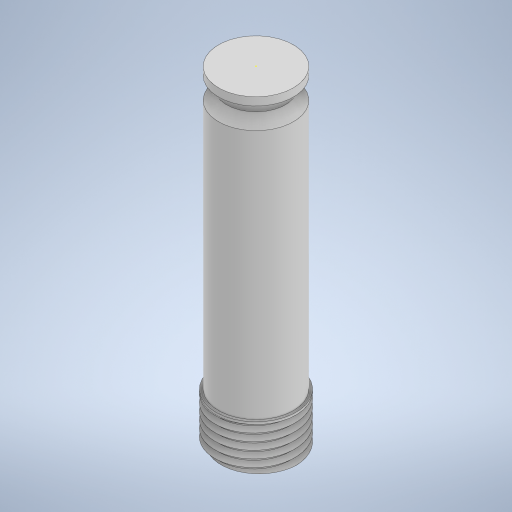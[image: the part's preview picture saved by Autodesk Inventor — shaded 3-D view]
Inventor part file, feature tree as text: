
AUTODESK INVENTOR PART (.ipt)
format: ipt  version: 2024 (Build 280153000, 153)  size: 430,080 bytes
history: native  units: mm
features: sketch x8, extrude x5, other x1, pattern_circular x1, revolve x1
ambient origin geometry x8: Origin, YZ Plane, XZ Plane, XY Plane, X Axis, Y Axis, Z Axis, Center Point
bodies: Volumenkörper1 (feature_tree)
feature tree (16):
  extrude  "Extrusion1"  Depth=61.0mm TaperAngle=0.0deg
  other  "Spirale1"
  extrude  "Extrusion9"  Depth=0.5mm
  extrude  "Extrusion6"  Depth=21.85mm
  pattern_circular  "Runde Anordnung1"  Count=4  [1 undecoded]
  extrude  "Extrusion10"  Depth=15.0mm
  extrude  "Extrusion11"  Depth=10.0mm
  revolve  "Umdrehung1"
  sketch  "Skizze18"  dims[d71=60.0deg d72=0.2mm d73=7.5mm d75=14.5mm d76=15.0mm d77=27.0mm d78=21.85mm d79=0.0mm d80=0.0mm d86=60.0mm d87=0.0mm d89=1.5mm d90=4.0mm d91=1.5mm d52=0.0mm d53=0.0mm d55=0.0mm]
  sketch  "Skizze1"  dims[d0=15.0mm d1=61.0mm d2=0.0mm]
  sketch  "Skizze6"  dims[d24=360.0deg d32=0.5mm]
  sketch  "Skizze8"  dims[d33=0.6mm d34=0.6mm d35=40.0mm d36=21.85mm d37=0.0mm d38=0.0mm]
  sketch  "Skizze12"  dims[d39=60.0mm d40=360.0deg d54=15.0mm]
  sketch  "Skizze14"  dims[d56=1.4mm]
  sketch  "Skizze15"  dims[d58=1.4mm d59=9.85mm d60=10.0mm d61=0.0mm d62=90.0deg d63=90.0deg d64=0.0mm d65=0.0mm d68=15.0mm]
  sketch  "Skizze17"  dims[d69=52.8mm d70=0.0mm]
note: 1 required parameter value undecoded (feature->parameter linkage not recoverable at this tier; creation-order binding heuristic only, values carry confidence <= 0.55)
